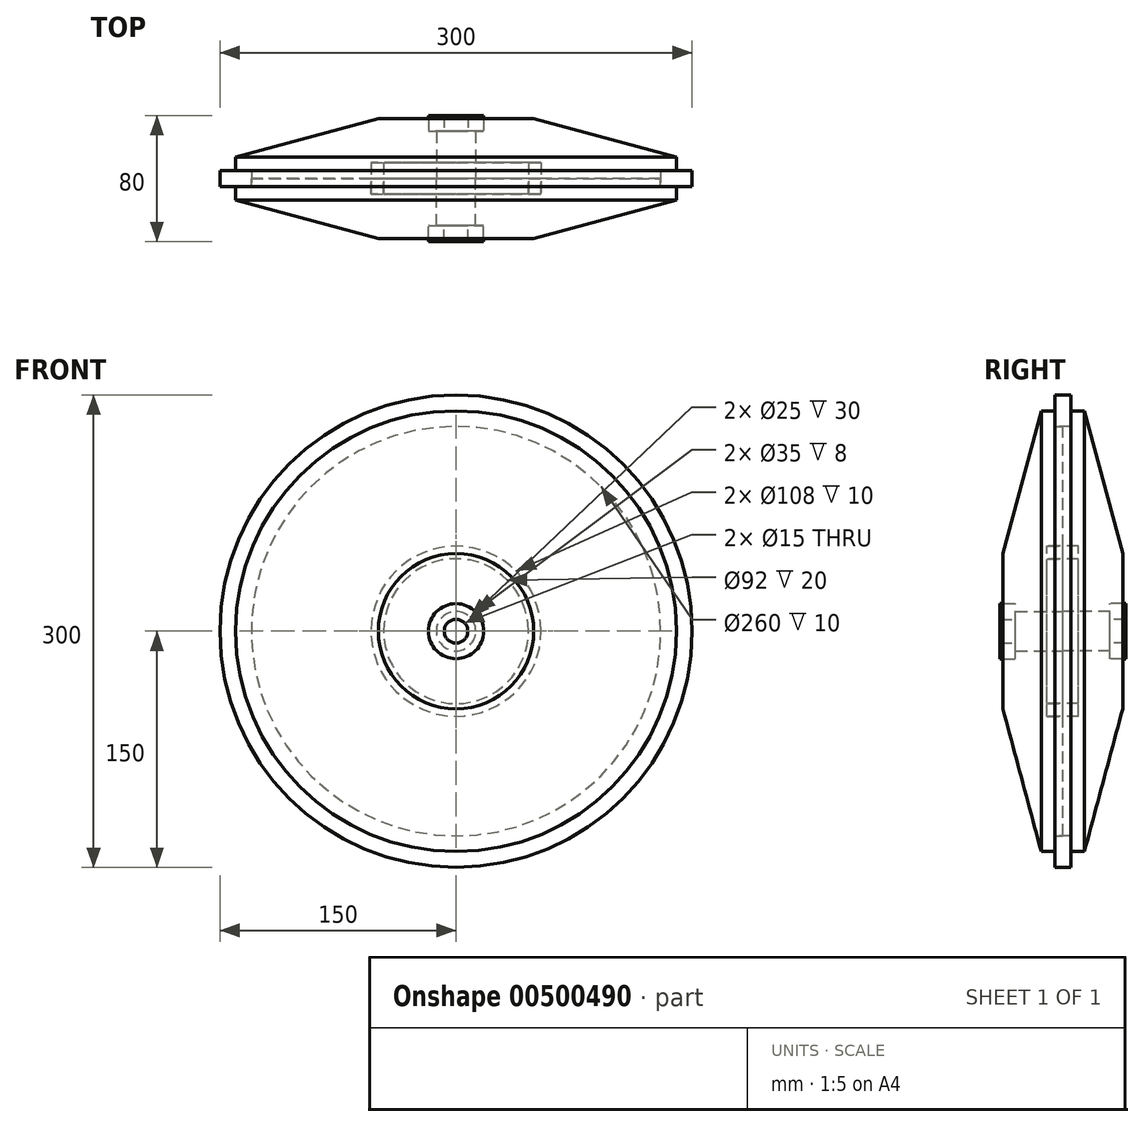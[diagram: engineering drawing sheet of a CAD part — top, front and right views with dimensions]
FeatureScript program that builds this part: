
annotation { "Feature Type Name" : "Feature", "Feature Type Description" : "" }
export const myFeature = defineFeature(function(context is Context, id is Id, definition is map)
    precondition{}
    {
        {
            var Q0;
            Q0=qCreatedBy(makeId("Top.planeOp"),FACE);
            var sketch = newSketch(context, id + "F0", { "sketchPlane" : qUnion([Q0])});
            skLineSegment(sketch, "E0.bottom", {"start": v(-7.5, 0) * mm, "end": v(7.5, 0) * mm, "construction": true});
            skLineSegment(sketch, "E0.top", {"start": v(-7.5, -54.85) * mm, "end": v(7.5, -54.85) * mm, "construction": true});
            skLineSegment(sketch, "E0.left", {"start": v(-7.5, 0) * mm, "end": v(-7.5, -54.85) * mm, "construction": true});
            skLineSegment(sketch, "E0.right", {"start": v(7.5, 0) * mm, "end": v(7.5, -54.85) * mm, "construction": true});
            skLineSegment(sketch, "E1", {"start": v(0, -54.85) * mm, "end": v(0, 0) * mm, "construction": true});
            skLineSegment(sketch, "E2", {"start": v(-150, -40) * mm, "end": v(-54, -40) * mm, "construction": true});
            skLineSegment(sketch, "E3.bottom", {"start": v(-150, -35) * mm, "end": v(-130, -35) * mm});
            skLineSegment(sketch, "E3.top", {"start": v(-150, -45) * mm, "end": v(-130, -45) * mm});
            skLineSegment(sketch, "E3.left", {"start": v(-150, -35) * mm, "end": v(-150, -45) * mm});
            skLineSegment(sketch, "E3.right", {"start": v(-130, -35) * mm, "end": v(-130, -45) * mm});
            skLineSegment(sketch, "E4.bottom", {"start": v(-7.5, 0) * mm, "end": v(-17.5, 0) * mm});
            skLineSegment(sketch, "E4.top", {"start": v(-7.5, -10) * mm, "end": v(-17.5, -10) * mm});
            skLineSegment(sketch, "E4.left", {"start": v(-7.5, 0) * mm, "end": v(-7.5, -10) * mm});
            skLineSegment(sketch, "E4.right", {"start": v(-17.5, 0) * mm, "end": v(-17.5, -10) * mm});
            skLineSegment(sketch, "E5", {"start": v(-140, -35) * mm, "end": v(-140, -26.3) * mm});
            skLineSegment(sketch, "E6", {"start": v(-140, -26.3) * mm, "end": v(-49.33, -2) * mm});
            skLineSegment(sketch, "E7", {"start": v(-49.33, -2) * mm, "end": v(-17.5, -2) * mm});
            skLineSegment(sketch, "E8", {"start": v(-17.5, -2) * mm, "end": v(-17.5, -10) * mm});
            skLineSegment(sketch, "E9", {"start": v(-12.5, -10) * mm, "end": v(-12.5, -40) * mm});
            skLineSegment(sketch, "E10", {"start": v(-12.5, -40) * mm, "end": v(-46, -40) * mm});
            skLineSegment(sketch, "E11", {"start": v(-130, -40) * mm, "end": v(-130, -35) * mm});
            skLineSegment(sketch, "E12.bottom", {"start": v(-54, -30) * mm, "end": v(-46, -30) * mm});
            skLineSegment(sketch, "E12.top", {"start": v(-54, -50) * mm, "end": v(-46, -50) * mm});
            skLineSegment(sketch, "E12.left", {"start": v(-54, -30) * mm, "end": v(-54, -50) * mm});
            skLineSegment(sketch, "E12.right", {"start": v(-46, -30) * mm, "end": v(-46, -50) * mm});
            skLineSegment(sketch, "E13.trimOffspring", {"start": v(-46, -40) * mm, "end": v(0, -40) * mm, "construction": true});
            skLineSegment(sketch, "E14.trimOffspring", {"start": v(-54, -40) * mm, "end": v(-130, -40) * mm});
            skSolve(sketch);
        }
        {
            var Q0;
            {var subQ0=sQuery(id+"F0.wireOp",EDGE,"E5");Q0=makeQuery(id+"F0.imprint","IMPRINT",FACE,{"disambiguationData":[TD([[makeQuery(id+"F0.imprint","IMPRINT",EDGE,{"derivedFrom":subQ0}),-1.0]])]});}
            var Q1;
            Q1=sQuery(id+"F0.wireOp",EDGE,"E1");
            revolve(context, id + "F1", {"entities" : qUnion([Q0]), "axis" : qUnion([Q1]), "revolveType" : RevolveType.FULL});
        }
        {
            var Q0;
            Q0=makeQuery(id+"F0.imprint","IMPRINT",FACE,{"disambiguationData":[TD([[makeQuery(id+"F0.imprint","IMPRINT",EDGE,{"derivedFrom":sQuery(id+"F0.wireOp",EDGE,"E3.top")}),1.0]])]});
            var Q1;
            Q1=sQuery(id+"F0.wireOp",EDGE,"E1");
            revolve(context, id + "F2", {"entities" : qUnion([Q0]), "axis" : qUnion([Q1]), "revolveType" : RevolveType.FULL});
        }
        {
            var Q0;
            Q0=makeQuery(id+"F0.imprint","IMPRINT",FACE,{"disambiguationData":[TD([[makeQuery(id+"F0.imprint","IMPRINT",EDGE,{"derivedFrom":sQuery(id+"F0.wireOp",EDGE,"E4.bottom")}),1.0]])]});
            var Q1;
            Q1=sQuery(id+"F0.wireOp",EDGE,"E1");
            revolve(context, id + "F3", {"entities" : qUnion([Q0]), "axis" : qUnion([Q1]), "revolveType" : RevolveType.FULL});
        }
        {
            var Q0;
            Q0=makeQuery(id+"F1.opRevolve","SWEPT_FACE",FACE,{"disambiguationData":[OSD([sQuery(id+"F0.wireOp",EDGE,"E14.trimOffspring")])]});
            var sketch = newSketch(context, id + "F4", { "sketchPlane" : qUnion([Q0])});
            skSolve(sketch);
        }
        {
            var Q0;
            {var subQ3=sQuery(id+"F0.wireOp",EDGE,"E12.bottom");Q0=makeQuery(id+"F0.imprint","IMPRINT",FACE,{"disambiguationData":[TD([[makeQuery(id+"F0.imprint","IMPRINT",EDGE,{"derivedFrom":subQ3}),-1.0]])]});}
            var Q1;
            Q1=sQuery(id+"F0.wireOp",EDGE,"E1");
            revolve(context, id + "F5", {"entities" : qUnion([Q0]), "axis" : qUnion([Q1]), "revolveType" : RevolveType.FULL});
        }
        {
            var Q0;
            Q0=makeQuery(id+"F1.opRevolve","SWEPT_BODY",BODY,{"disambiguationData":[OSD([sQuery(id+"F0.wireOp",EDGE,"E3.bottom"),sQuery(id+"F0.wireOp",EDGE,"E4.top"),sQuery(id+"F0.wireOp",EDGE,"E5"),sQuery(id+"F0.wireOp",EDGE,"E6"),sQuery(id+"F0.wireOp",EDGE,"E7"),sQuery(id+"F0.wireOp",EDGE,"E8"),sQuery(id+"F0.wireOp",EDGE,"E9"),sQuery(id+"F0.wireOp",EDGE,"E10"),sQuery(id+"F0.wireOp",EDGE,"E11"),sQuery(id+"F0.wireOp",EDGE,"E12.bottom"),sQuery(id+"F0.wireOp",EDGE,"E12.left"),sQuery(id+"F0.wireOp",EDGE,"E12.right"),sQuery(id+"F0.wireOp",EDGE,"E14.trimOffspring")])]});
            var Q1;
            Q1=makeQuery(id+"F3.opRevolve","SWEPT_BODY",BODY,{"disambiguationData":[OSD([sQuery(id+"F0.wireOp",EDGE,"E4.bottom"),sQuery(id+"F0.wireOp",EDGE,"E4.top"),sQuery(id+"F0.wireOp",EDGE,"E4.left"),sQuery(id+"F0.wireOp",EDGE,"E4.right"),sQuery(id+"F0.wireOp",EDGE,"E8")])]});
            var Q2;
            {var subQ0=sQuery(id+"F0.wireOp",EDGE,"E14.trimOffspring");Q2=makeQuery(id+"F4.imprint","IMPRINT",FACE,{"disambiguationData":[TD([[makeQuery(id+"F4.imprint","IMPRINT",EDGE,{"derivedFrom":makeQuery(id+"F1.opRevolve","SWEPT_EDGE",EDGE,{"disambiguationData":[OSD([sQuery(id+"F0.wireOp",EDGE,"E12.left"),subQ0])]})}),-1.0]])]});}
            mirror(context, id + "F6", {"entities" : qUnion([Q0, Q1]), "mirrorPlane" : qUnion([Q2])});
        }
    });
